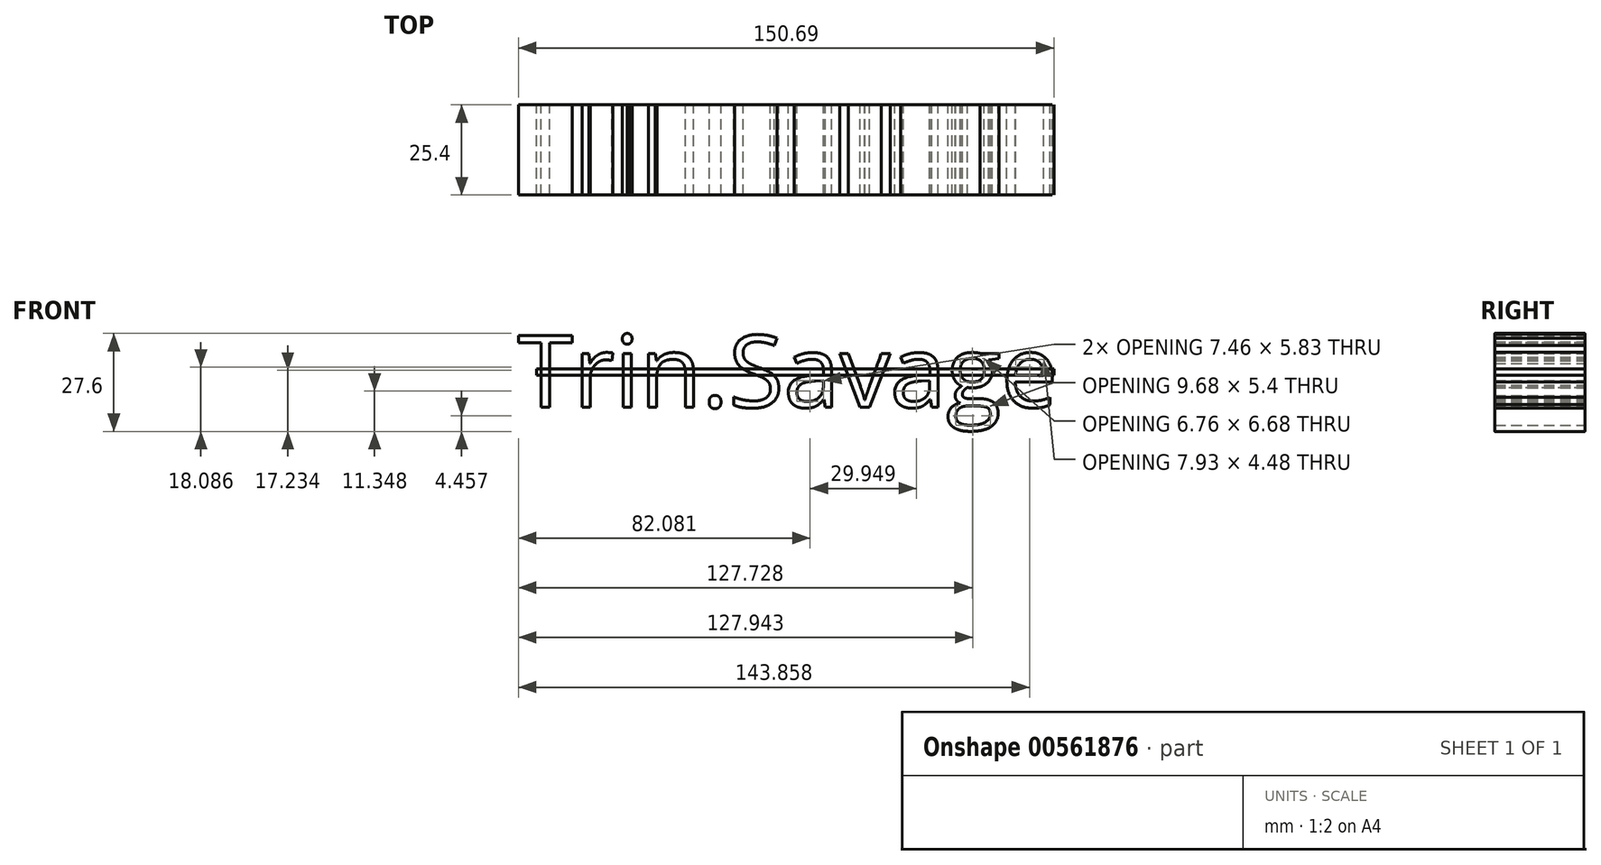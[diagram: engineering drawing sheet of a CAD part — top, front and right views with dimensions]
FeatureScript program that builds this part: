
annotation { "Feature Type Name" : "Feature", "Feature Type Description" : "" }
export const myFeature = defineFeature(function(context is Context, id is Id, definition is map)
    precondition{}
    {
        {
            var Q0;
            Q0=qCreatedBy(makeId("Front.planeOp"),FACE);
            var sketch = newSketch(context, id + "F0", { "sketchPlane" : qUnion([Q0])});
            skText(sketch, "E0", { "text": "Trin.Savage", "fontName": "OpenSans-Regular.ttf"});
            const initialGuessF0  = {"E0": [-0.00537, -0.0349, 1, 0, 0.0204]};
            skSetInitialGuess(sketch, initialGuessF0);
            skSolve(sketch);
        }
        {
            var Q0;
            Q0 = qSketchRegion(id + "F0", true);
            extrude(context, id + "F1", {"entities" : qUnion([Q0]), "depth" : 25.4 * mm, "offsetDistance" : 25.4 * mm});
        }
        {
            var Q0;
            Q0=qCreatedBy(makeId("Front.planeOp"),FACE);
            var sketch = newSketch(context, id + "F2", { "sketchPlane" : qUnion([Q0])});
            skLineSegment(sketch, "E1.bottom", {"start": v(0, -24.05) * mm, "end": v(145.57, -24.05) * mm});
            skLineSegment(sketch, "E1.top", {"start": v(0, -25.93) * mm, "end": v(145.57, -25.93) * mm});
            skLineSegment(sketch, "E1.left", {"start": v(0, -24.05) * mm, "end": v(0, -25.93) * mm});
            skLineSegment(sketch, "E1.right", {"start": v(145.57, -24.05) * mm, "end": v(145.57, -25.93) * mm});
            skSolve(sketch);
        }
        {
            var Q0;
            Q0 = qSketchRegion(id + "F2", true);
            extrude(context, id + "F3", {"entities" : qUnion([Q0]), "depth" : 25.4 * mm, "offsetDistance" : 25.4 * mm});
        }
    });
